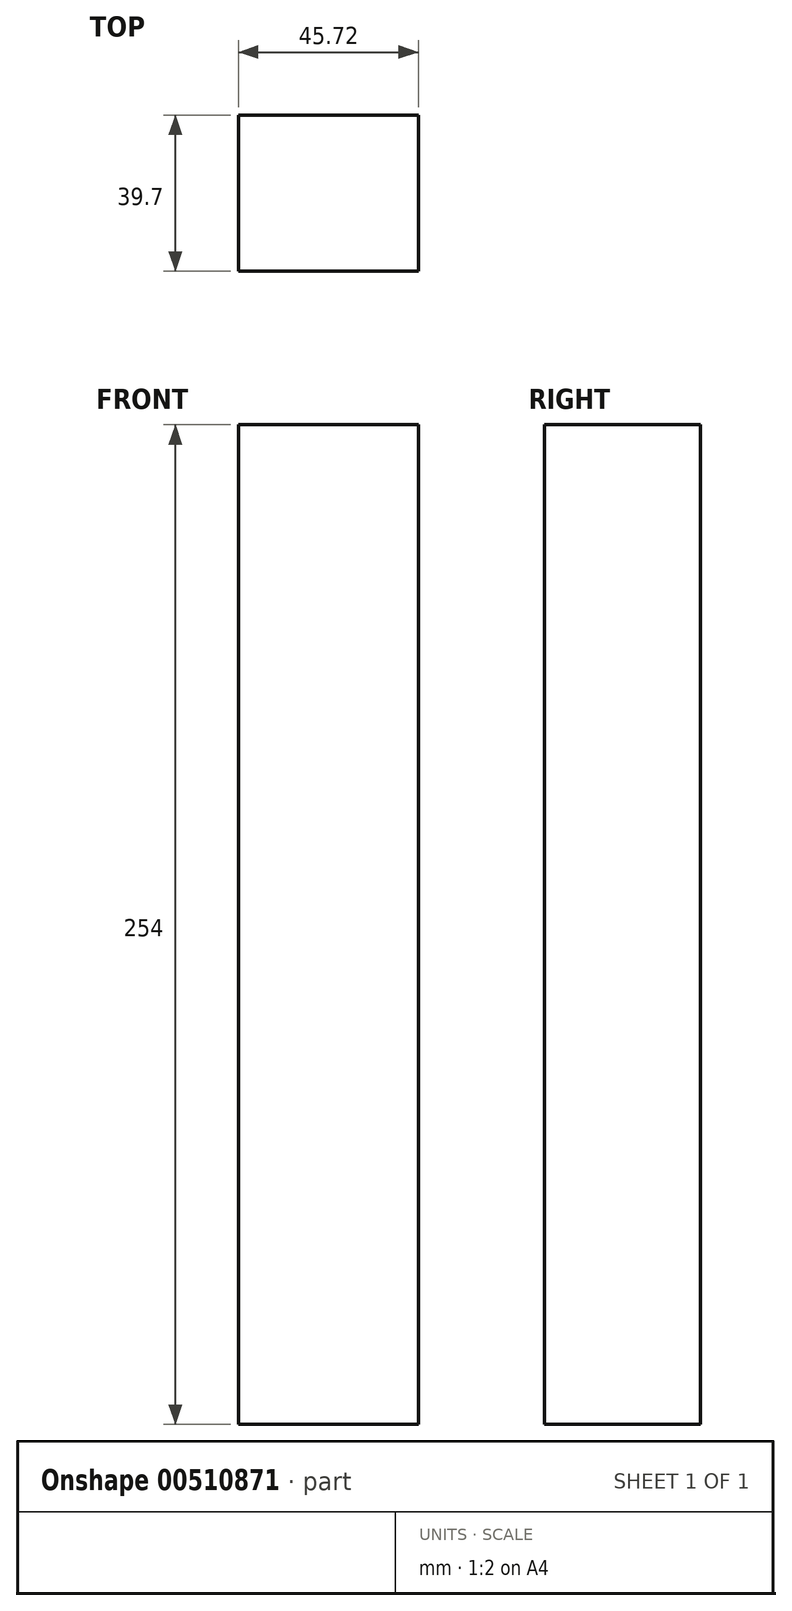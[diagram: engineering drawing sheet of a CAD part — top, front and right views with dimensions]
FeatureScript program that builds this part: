
annotation { "Feature Type Name" : "Feature", "Feature Type Description" : "" }
export const myFeature = defineFeature(function(context is Context, id is Id, definition is map)
    precondition{}
    {
        {
            var Q0;
            Q0=qCreatedBy(makeId("Top.planeOp"),FACE);
            var sketch = newSketch(context, id + "F0", { "sketchPlane" : qUnion([Q0])});
            skLineSegment(sketch, "E0.bottom", {"start": v(-25.27, 3.91) * mm, "end": v(-70.99, 3.91) * mm});
            skLineSegment(sketch, "E0.top", {"start": v(-25.27, 43.61) * mm, "end": v(-70.99, 43.61) * mm});
            skLineSegment(sketch, "E0.left", {"start": v(-25.27, 3.91) * mm, "end": v(-25.27, 43.61) * mm});
            skLineSegment(sketch, "E0.right", {"start": v(-70.99, 3.91) * mm, "end": v(-70.99, 43.61) * mm});
            skPoint(sketch, "E0.middle", {"position": v(-48.13, 23.76) * mm});
            skSolve(sketch);
        }
        {
            var Q0;
            Q0 = qSketchRegion(id + "F0", true);
            extrude(context, id + "F1", {"entities" : qUnion([Q0]), "depth" : 254 * mm});
        }
    });
